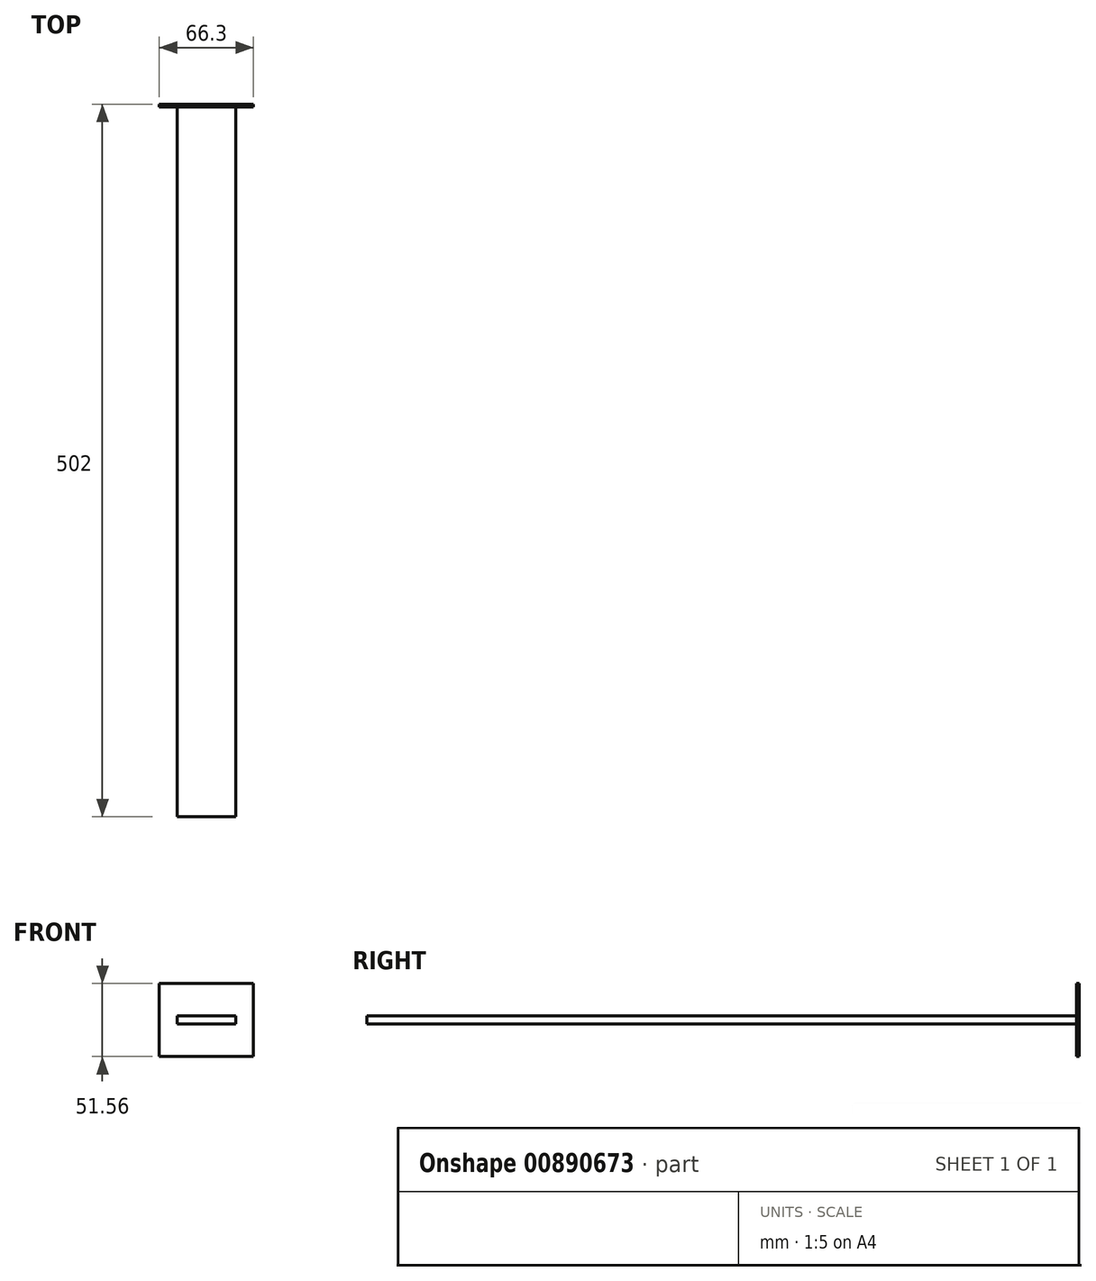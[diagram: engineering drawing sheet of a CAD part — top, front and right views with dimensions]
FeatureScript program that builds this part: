
annotation { "Feature Type Name" : "Feature", "Feature Type Description" : "" }
export const myFeature = defineFeature(function(context is Context, id is Id, definition is map)
    precondition{}
    {
        {
            var Q0;
            Q0=qCreatedBy(makeId("Front.planeOp"),FACE);
            var sketch = newSketch(context, id + "F0", { "sketchPlane" : qUnion([Q0])});
            skLineSegment(sketch, "E0.bottom", {"start": v(-33.15, 25.78) * mm, "end": v(33.15, 25.78) * mm});
            skLineSegment(sketch, "E0.top", {"start": v(-33.15, -25.78) * mm, "end": v(33.15, -25.78) * mm});
            skLineSegment(sketch, "E0.left", {"start": v(-33.15, 25.78) * mm, "end": v(-33.15, -25.78) * mm});
            skLineSegment(sketch, "E0.right", {"start": v(33.15, 25.78) * mm, "end": v(33.15, -25.78) * mm});
            skPoint(sketch, "E0.middle", {"position": v(0, 0) * mm});
            skSolve(sketch);
        }
        {
            var Q0;
            Q0=makeQuery(id+"F0.imprint","IMPRINT",FACE,{"disambiguationData":[TD([[makeQuery(id+"F0.imprint","IMPRINT",EDGE,{"derivedFrom":sQuery(id+"F0.wireOp",EDGE,"E0.bottom")}),-1.0]])]});
            extrude(context, id + "F1", {"entities" : qUnion([Q0]), "depth" : 2 * mm, "offsetDistance" : 25.4 * mm});
        }
        {
            var Q0;
            Q0=makeQuery(id+"F1.opExtrude","CAP_FACE",FACE,{"disambiguationData":[OSD([sQuery(id+"F0.wireOp",EDGE,"E0.bottom"),sQuery(id+"F0.wireOp",EDGE,"E0.top"),sQuery(id+"F0.wireOp",EDGE,"E0.left"),sQuery(id+"F0.wireOp",EDGE,"E0.right")])],"isStart":false});
            var sketch = newSketch(context, id + "F2", { "sketchPlane" : qUnion([Q0])});
            skLineSegment(sketch, "E1.bottom", {"start": v(-20.7, 2.92) * mm, "end": v(20.7, 2.92) * mm});
            skLineSegment(sketch, "E1.top", {"start": v(-20.7, -2.92) * mm, "end": v(20.7, -2.92) * mm});
            skLineSegment(sketch, "E1.left", {"start": v(-20.7, 2.92) * mm, "end": v(-20.7, -2.92) * mm});
            skLineSegment(sketch, "E1.right", {"start": v(20.7, 2.92) * mm, "end": v(20.7, -2.92) * mm});
            skPoint(sketch, "E1.middle", {"position": v(0, 0) * mm});
            skSolve(sketch);
        }
        {
            var Q0;
            Q0=makeQuery(id+"F2.imprint","IMPRINT",FACE,{"disambiguationData":[TD([[makeQuery(id+"F2.imprint","IMPRINT",EDGE,{"derivedFrom":sQuery(id+"F2.wireOp",EDGE,"E1.bottom")}),-1.0]])]});
            extrude(context, id + "F3", {"entities" : qUnion([Q0]), "depth" : 500 * mm, "offsetDistance" : 25.4 * mm});
        }
    });
